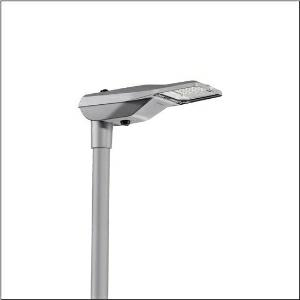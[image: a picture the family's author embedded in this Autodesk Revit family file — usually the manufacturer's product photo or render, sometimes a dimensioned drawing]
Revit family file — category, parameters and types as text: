
# Revit family: streetlight_sl_21_iq_micro___st1_0a_5xe1d61y08db_6c32
name_source: partatom
category: Lighting Fixtures
units: mm (PartAtom-declared; Revit-internal decimal feet)

## family parameters
Cut with Voids When Loaded = No
Host = Face
Light Source = No
Part Type = Normal
Room Calculation Point = No
Round Connector Dimension = Use Diameter
Shared = No

## types (1)
- --- (1 x LED, 4430 lm, 39.1 W, 2700K)
    Apparent Load = 39 VA
    CIE Flux Codes = 37 72 97 100 100
    Color Rendering = 70
    Color Temperature = 2700K
    Default Elevation = 1800 mm
    Description = Streetlight SL 21 iQ micro, mast luminaire, primary light control with lens, of PMMA, primary optical cover: cover, of toughened safety glass, transparent, light distribution: ST1.0a, light emission: direct distribution, primary light characteristic: asymmetric, installation type: post-top, side-entry, LED, High Power LED, rated luminous flux: 4.430lm, luminous efficacy: 113lm/W, light colour: 727, colour temperature: 2700K, control gear: iQ-Street Remote, D4i with power reduction, control: pre-setting: logarithmic dimming characteristic, Street-Remote, Auto-Match, Temp-Guard, Lumen-Switch, Night-Set, Smart-Wire, Light-Fading, Desk-Remote (wireless, voltage-free reading and setting of iQ features in the workshop via application-optimized NFC function/RFID function), optimised constant luminous flux control (CLO 2.0), mains connection: 220..240V, AC, 50/60Hz, start of lifetime: 39W, end of service life: 41W, reduction: 17W, luminaire housing, of diecast aluminium, powder-coated, SITECO metallic grey (DB 702S), corrosivity category C5 high according to DIN EN ISO 12944, please order mast flange separately, inclination adjustable: 0°, 5°, 10°, 15°, sealing non-destructively replaceable, multi-level sealing system, length: 528mm, width: 235mm, height: 110mm, mast flange for spigot size: 42mm (side-entry): 5XC10008XM4, 60/48mm (side-entry/post-top): 5XC10108XM2, 76/60mm (side-entry/post-top): 5XC10108XM1, mounting height: 4..8m, Smart Interface below and above, protection rating (complete): IP66, insulation class (complete): insulation class II (safety insulation), certification: CE, ENEC, ENEC+, VDE, impact resistance: IK10, permissible operating ambient temperature for outdoor applications: -40..+50°C, standard-compliant lighting for roads and squares, packaging unit: 1 piece

Light Distribution: ST1.0a
    Height = 110 mm
    Lamp = 1 x LED
    Lamp Light Flux = 4430 lm
    Lamp Power = 39.1 W
    Lamp count = 1
    Length = 528 mm
    Luminous efficacy = 113 lm/W
    Manufacturer = Siteco
    ModVariant = No
    Model = 5XE1D61Y08DB
    Number of Poles = 1
    OnlyDefault = Yes
    Power Factor = 1
    Product Name = Streetlight SL 21 iQ micro | ST1.0a
    Product group = mast luminaire | pylon top
    ProductGroupID = 6100
    Protection Class = Protection class II
    Protection Degree = IP 66
    RLX_Detail_Level = 1
    RLX_Emergency_Light_Flux = 0 lm
    RLX_Emergency_Type = 0
    RLX_Emergency_Type_DB = No
    RlxData = <blob elided: 98801 chars, md5=751983de>
    Socket = socket
    Standby Power = 0 W
    System Light Flux = 4430 lm
    System Power = 39 W
    Type Comments = factory setting: luminous flux: 100 % | dim-lin: 254 | 765 mA
    Type Image = l_1007239.jpg
    URL = http://relux.com
    VarID = @adj_115617
    Voltage = 0 V
    Weight = 0.00 kg
    Width = 235 mm

## geometry (parser evidence)
native form markers: Blend x4, Sweep x10
no freeform markers — native parametric forms only
